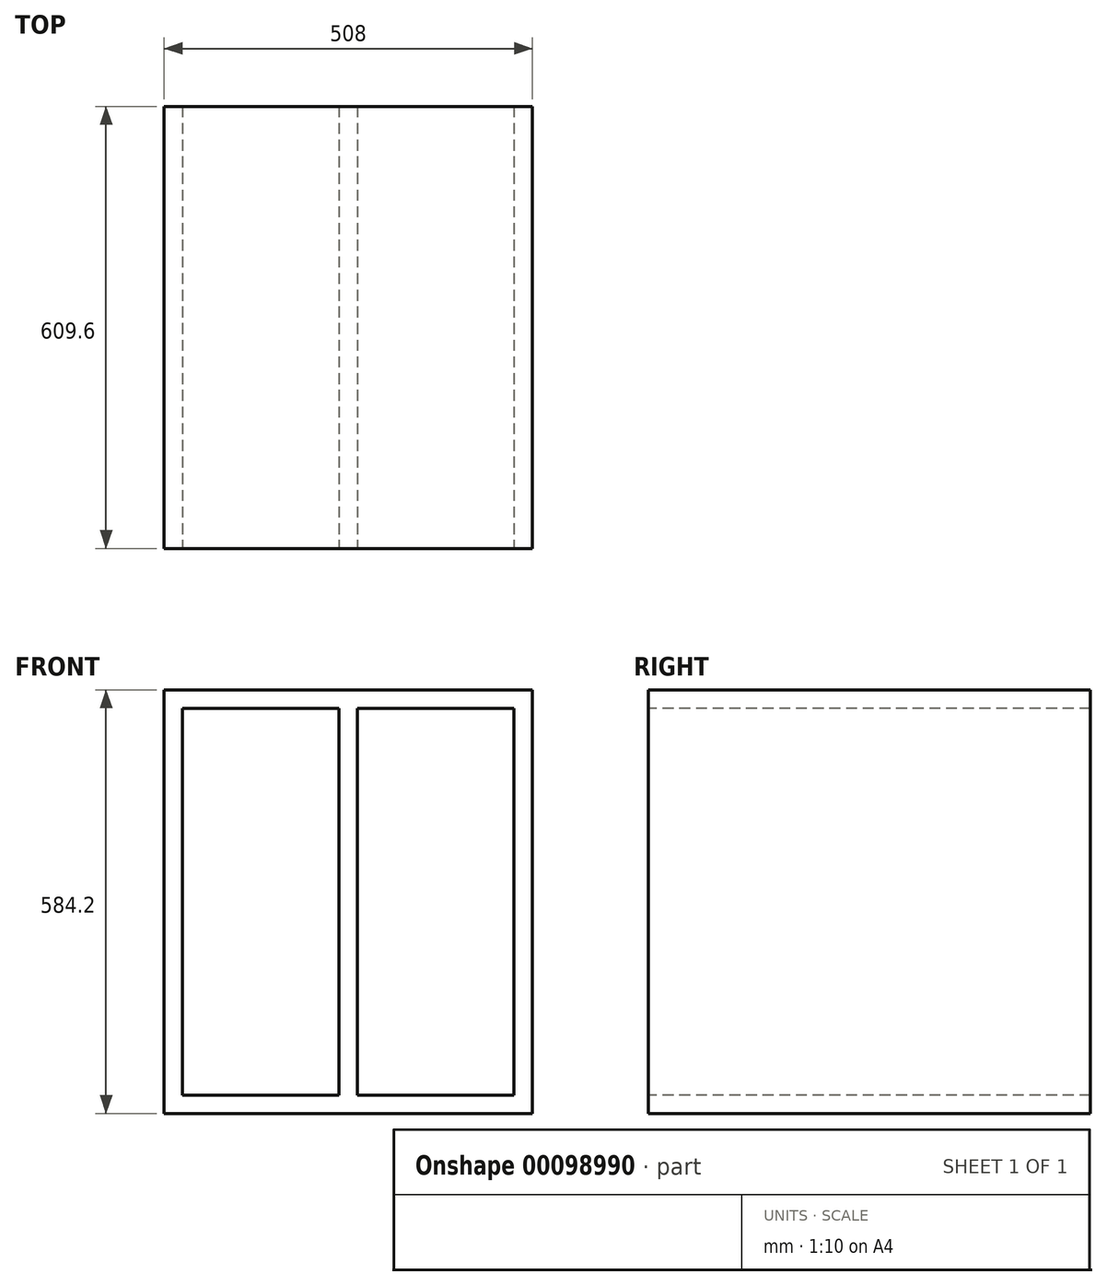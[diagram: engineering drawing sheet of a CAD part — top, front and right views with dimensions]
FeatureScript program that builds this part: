
annotation { "Feature Type Name" : "Feature", "Feature Type Description" : "" }
export const myFeature = defineFeature(function(context is Context, id is Id, definition is map)
    precondition{}
    {
        {
            var Q0;
            Q0=qCreatedBy(makeId("Front.planeOp"),FACE);
            var sketch = newSketch(context, id + "F0", { "sketchPlane" : qUnion([Q0])});
            skLineSegment(sketch, "E0.bottom", {"start": v(0, 0) * mm, "end": v(228.6, 0) * mm});
            skLineSegment(sketch, "E0.top", {"start": v(0, 584.2) * mm, "end": v(228.6, 584.2) * mm});
            skLineSegment(sketch, "E0.left", {"start": v(0, 0) * mm, "end": v(0, 584.2) * mm});
            skLineSegment(sketch, "E1", {"start": v(228.6, 584.2) * mm, "end": v(457.2, 584.2) * mm});
            skLineSegment(sketch, "E2", {"start": v(457.2, 584.2) * mm, "end": v(457.2, 0) * mm});
            skLineSegment(sketch, "E3", {"start": v(457.2, 0) * mm, "end": v(228.6, 0) * mm});
            skLineSegment(sketch, "E4", {"start": v(0, 584.2) * mm, "end": v(-25.4, 584.2) * mm});
            skLineSegment(sketch, "E5", {"start": v(-25.4, 584.2) * mm, "end": v(-25.4, 0) * mm});
            skLineSegment(sketch, "E6", {"start": v(-25.4, 0) * mm, "end": v(0, 0) * mm});
            skLineSegment(sketch, "E7", {"start": v(0, 25.4) * mm, "end": v(215.9, 25.4) * mm});
            skLineSegment(sketch, "E8", {"start": v(0, 558.8) * mm, "end": v(215.9, 558.8) * mm});
            skLineSegment(sketch, "E9", {"start": v(457.2, 584.2) * mm, "end": v(482.6, 584.2) * mm});
            skLineSegment(sketch, "E10", {"start": v(482.6, 584.2) * mm, "end": v(482.6, 0) * mm});
            skLineSegment(sketch, "E11", {"start": v(482.6, 0) * mm, "end": v(457.2, 0) * mm});
            skLineSegment(sketch, "E12", {"start": v(215.9, 558.8) * mm, "end": v(215.9, 571.5) * mm});
            skLineSegment(sketch, "E13", {"start": v(215.9, 571.5) * mm, "end": v(241.3, 571.5) * mm});
            skLineSegment(sketch, "E14", {"start": v(241.3, 571.5) * mm, "end": v(241.3, 558.8) * mm});
            skLineSegment(sketch, "E15", {"start": v(215.9, 25.4) * mm, "end": v(215.9, 12.7) * mm});
            skLineSegment(sketch, "E16", {"start": v(215.9, 12.7) * mm, "end": v(241.3, 12.7) * mm});
            skLineSegment(sketch, "E17", {"start": v(241.3, 12.7) * mm, "end": v(241.3, 25.4) * mm});
            skLineSegment(sketch, "E18.trimOffspring", {"start": v(241.3, 558.8) * mm, "end": v(457.2, 558.8) * mm});
            skLineSegment(sketch, "E19.trimOffspring", {"start": v(241.3, 25.4) * mm, "end": v(457.2, 25.4) * mm});
            skLineSegment(sketch, "E20", {"start": v(215.9, 558.8) * mm, "end": v(215.9, 25.4) * mm});
            skLineSegment(sketch, "E21", {"start": v(241.3, 558.8) * mm, "end": v(241.3, 25.4) * mm});
            skSolve(sketch);
        }
        {
            var Q0;
            {var subQ0=sQuery(id+"F0.wireOp",EDGE,"E9");Q0=makeQuery(id+"F0.imprint","IMPRINT",FACE,{"disambiguationData":[TD([[makeQuery(id+"F0.imprint","IMPRINT",EDGE,{"derivedFrom":subQ0}),-1.0]])]});}
            var Q1;
            {var subQ4=sQuery(id+"F0.wireOp",EDGE,"E0.top");Q1=makeQuery(id+"F0.imprint","IMPRINT",FACE,{"disambiguationData":[TD([[makeQuery(id+"F0.imprint","IMPRINT",EDGE,{"derivedFrom":subQ4}),-1.0]])]});}
            var Q2;
            {var subQ0=sQuery(id+"F0.wireOp",EDGE,"E4");Q2=makeQuery(id+"F0.imprint","IMPRINT",FACE,{"disambiguationData":[TD([[makeQuery(id+"F0.imprint","IMPRINT",EDGE,{"derivedFrom":subQ0}),1.0]])]});}
            var Q3;
            Q3=makeQuery(id+"F0.imprint","IMPRINT",FACE,{"disambiguationData":[TD([[makeQuery(id+"F0.imprint","IMPRINT",EDGE,{"derivedFrom":sQuery(id+"F0.wireOp",EDGE,"E12")}),-1.0]])]});
            var Q4;
            {var subQ2=sQuery(id+"F0.wireOp",EDGE,"E0.bottom");Q4=makeQuery(id+"F0.imprint","IMPRINT",FACE,{"disambiguationData":[TD([[makeQuery(id+"F0.imprint","IMPRINT",EDGE,{"derivedFrom":subQ2}),1.0]])]});}
            extrude(context, id + "F1", {"entities" : qUnion([Q0, Q1, Q2, Q3, Q4]), "oppositeDirection" : true, "depth" : 609.6 * mm});
        }
    });
